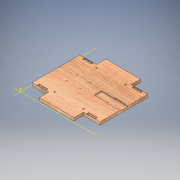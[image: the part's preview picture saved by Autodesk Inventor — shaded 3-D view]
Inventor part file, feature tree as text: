
AUTODESK INVENTOR PART (.ipt)
format: ipt  version: 2017 (Build 210142000, 142)  size: 321,536 bytes
history: native  units: in
note: dims shown in document units (in); Inventor stores cm internally (conversion verified against a paired STEP export)
features: sketch x6, extrude x5, plane x1, projected_geometry x1
ambient origin geometry x8: Origin, YZ Plane, XZ Plane, XY Plane, X Axis, Y Axis, Z Axis, Center Point
bodies: Solid1 (feature_tree)
feature tree (13):
  extrude  "Extrusion1"  Depth=0.5in TaperAngle=0.0deg
  plane  "Work Plane1"
  extrude  "Extrusion2"  Depth=1.5in
  extrude  "Extrusion3"  Depth=4.5in
  extrude  "Extrusion4"  Depth=1.25in
  sketch  "Sketch9"  dims[d65=0.625in d66=1.25in]
  extrude  "Extrusion5"  Depth=1.5in
  sketch  "Sketch2"  dims[d5=0.7874in d7=0.7874in d8=12.0in d9=12.0in d10=6.0in d11=11.5in d12=11.75in d13=8.25in d14=0.5in d15=0.5in d16=0.25in d17=5.0in d18=7.25in d19=0.5in d20=0.0in]
  sketch  "Sketch6"  dims[d34=0.5in]
  sketch  "Sketch7"  dims[d49=12.0in d50=12.0in d51=6.0in d52=11.5in d53=11.75in d54=8.25in d55=0.5in d56=0.5in d57=0.25in d58=5.0in d59=7.25in d62=1.5in]
  projected_geometry  "Projected Loop1"
  sketch  "Sketch8"  dims[d63=0.325in d64=4.5in]
  sketch  "Sketch10"  dims[d67=0.325in d68=1.5in d69=0.125in d70=0.0in d71=4.5in d72=0.625in d73=0.325in d74=0.125in d75=1.1811in d77=0.75in d78=0.7874in d80=1.375in d83=0.5in d84=0.0in d85=4.5in d86=180.0deg d87=0.125in d88=0.0in d89=0.125in d90=0.0in]
